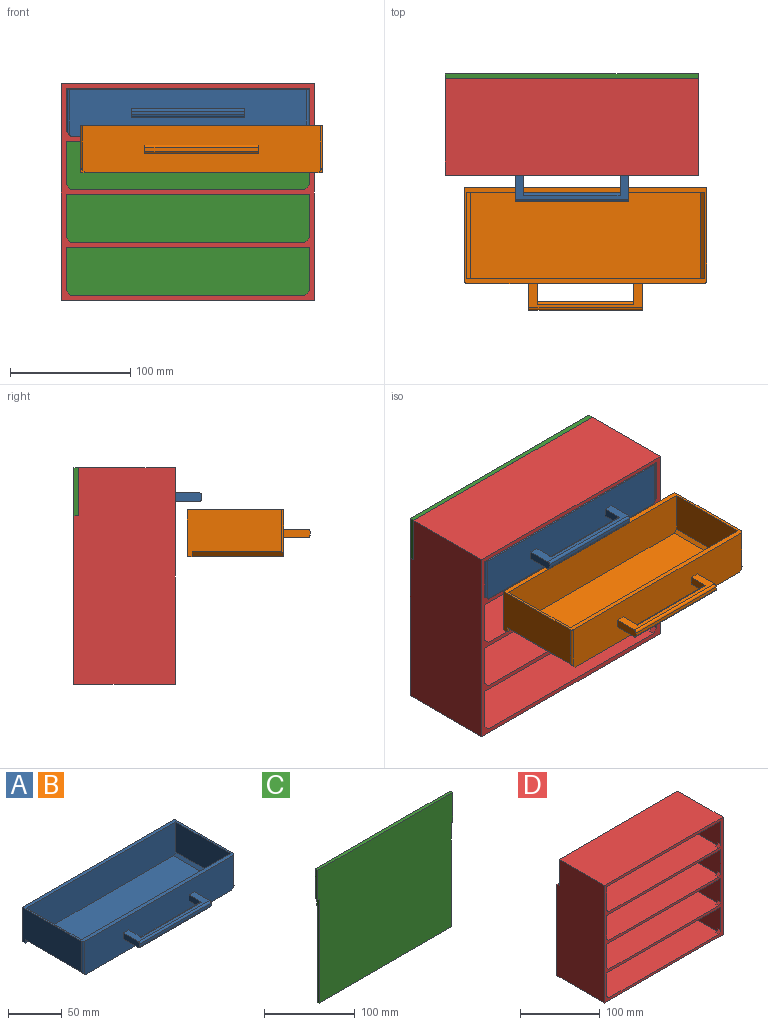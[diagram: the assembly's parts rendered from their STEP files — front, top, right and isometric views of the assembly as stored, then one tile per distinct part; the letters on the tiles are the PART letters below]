
ASSEMBLY  parts=4 mates=2
PART A: 31 faces, bbox 201x102x39 mm
  f0: plane 17x7mm, normal (1,0,0), area 106.7mm2, adj f2,f22,f23,f26,f27,f28
  f1: plane 17x7mm, normal (-1,0,0), area 106.7mm2, adj f2,f22,f23,f26,f27,f28
  f2: plane 197x39mm, normal (0,-1,0), area 7581mm2, adj f0,f1,f8,f10,f11,f12,f19,f20
  f3: plane 72x34.17mm, normal (-1,0,0), area 2460mm2, adj f4,f8,f15,f18
  f4: plane 72x2.83mm, normal (-0.71,0,0.71), area 288.5mm2, adj f3,f5,f15,f18
  f5: plane 191.33x72mm, normal (0,0,1), area 13776mm2, adj f4,f6,f15,f18
  f6: plane 72x2.83mm, normal (0.71,0,0.71), area 288.5mm2, adj f5,f7,f15,f18
  f7: plane 72x34.17mm, normal (1,0,0), area 2460mm2, adj f6,f8,f15,f18
  f8: plane 201x80mm, normal (0,0,1), area 1894.3mm2, adj f2,f3,f7,f9,f13,f15,f16,f18
  f9: plane 78x39mm, normal (-1,0,0), area 2745.6mm2, adj f8,f10,f11,f16,f17,f19
  f10: plane 76x4.01mm, normal (-0.71,0,-0.71), area 429.2mm2, adj f2,f9,f11,f17,f19
  f11: plane 201x80mm, normal (0,0,-1), area 15471.2mm2, adj f2,f9,f10,f12,f13,f14,f16,f17
  f12: plane 76x4.01mm, normal (0.71,0,-0.71), area 429.2mm2, adj f2,f11,f13,f14,f20
  f13: plane 78x39mm, normal (1,0,0), area 2745.6mm2, adj f8,f11,f12,f14,f16,f20
  f14: plane 4.01x4.01mm, normal (0,-1,0), area 8mm2, adj f11,f12,f13
  f15: plane 197x37mm, normal (0,-1,0), area 7281mm2, adj f3,f4,f5,f6,f7,f8
  f16: plane 201x39mm, normal (0,1,0), area 7839mm2, adj f8,f9,f11,f13
  f17: plane 4.01x4.01mm, normal (0,-1,0), area 8mm2, adj f9,f10,f11
  f18: plane 197x37mm, normal (0,1,0), area 7281mm2, adj f3,f4,f5,f6,f7,f8
  f19: cylinder r=2mm len=37mm, axis (0,0,1), area 112.2mm2, adj f2,f8,f9,f10
  f20: cylinder r=2mm len=37mm, axis (0,0,-1), area 112.2mm2, adj f2,f8,f12,f13
  f21: plane 22x7mm, normal (-1,0,0), area 152.3mm2, adj f2,f22,f23,f24,f29,f30
  f22: plane 94x20mm, normal (0,0,-1), area 520mm2, adj f0,f1,f2,f21,f25,f28,f29
  f23: plane 94x20mm, normal (0,0,1), area 520mm2, adj f0,f1,f2,f21,f25,f27,f30
  f24: plane 94x3mm, normal (0,-1,0), area 282mm2, adj f21,f25,f29,f30
  f25: plane 22x7mm, normal (1,0,0), area 152.3mm2, adj f2,f22,f23,f24,f29,f30
  f26: plane 80x3mm, normal (0,1,0), area 240mm2, adj f0,f1,f27,f28
  f27: cylinder r=2mm len=80mm, axis (-1,0,0), area 251.3mm2, adj f0,f1,f23,f26
  f28: cylinder r=2mm len=80mm, axis (1,0,0), area 251.3mm2, adj f0,f1,f22,f26
  f29: cylinder r=2mm len=94mm, axis (-1,0,0), area 295.3mm2, adj f21,f22,f24,f25
  f30: cylinder r=2mm len=94mm, axis (1,0,0), area 295.3mm2, adj f21,f23,f24,f25
PART B: same geometry as A
PART C: 16 faces, bbox 210x4x180 mm
  f0: plane 4x2.01mm, normal (0,0,-1), area 8mm2, adj f3,f5,f6,f11
  f1: plane 40x4mm, normal (-1,0,0), area 160mm2, adj f2,f4,f5,f6
  f2: plane 4x2.01mm, normal (0,0,-1), area 8mm2, adj f1,f5,f6,f12
  f3: plane 40x4mm, normal (1,0,0), area 160mm2, adj f0,f4,f5,f6
  f4: plane 210x4mm, normal (0,0,1), area 840mm2, adj f1,f3,f5,f6
  f5: plane 210x180mm, normal (0,-1,0), area 37238.6mm2, adj f0,f1,f2,f3,f4,f11,f12,f13
  f6: plane 210x180mm, normal (0,1,0), area 36718.6mm2, adj f0,f1,f2,f3,f4,f8,f9,f11
  f7: plane 130x2mm, normal (0,1,0), area 260mm2, adj f8,f12,f13,f15
  f8: plane 130x2mm, normal (-1,0,0), area 259.3mm2, adj f6,f7,f13,f15
  f9: plane 130x2mm, normal (1,0,0), area 259.3mm2, adj f6,f10,f13,f14
  f10: plane 130x2mm, normal (0,1,0), area 260mm2, adj f9,f11,f13,f14
  f11: plane 140x4mm, normal (1,0,0), area 300.7mm2, adj f0,f5,f6,f10,f13,f14
  f12: plane 140x4mm, normal (-1,0,0), area 300.7mm2, adj f2,f5,f6,f7,f13,f15
  f13: plane 205.99x4mm, normal (0,0,-1), area 816mm2, adj f5,f6,f7,f8,f9,f10,f11,f12
  f14: plane 2x2mm, normal (0,0,-1), area 4mm2, adj f6,f9,f10,f11
  f15: plane 2x2mm, normal (0,0,-1), area 4mm2, adj f6,f7,f8,f12
PART D: 50 faces, bbox 210x84x180 mm
  f0: plane 80x40mm, normal (-1,0,0), area 3180mm2, adj f7,f8,f13,f21,f48,f49
  f1: plane 80x40mm, normal (-1,0,0), area 3180mm2, adj f2,f8,f15,f21,f46,f47
  f2: plane 202x80mm, normal (0,0,1), area 16120mm2, adj f1,f8,f14,f21,f44,f45,f46,f47
  f3: plane 80x40mm, normal (-1,0,0), area 3180mm2, adj f6,f8,f17,f21,f42,f43
  f4: plane 80x40mm, normal (-1,0,0), area 3180mm2, adj f5,f8,f19,f21,f40,f41
  f5: plane 202x80mm, normal (0,0,1), area 16120mm2, adj f4,f8,f18,f21,f38,f39,f40,f41
  f6: plane 202x80mm, normal (0,0,1), area 16120mm2, adj f3,f8,f16,f21,f36,f37,f42,f43
  f7: plane 202x80mm, normal (0,0,1), area 16120mm2, adj f0,f8,f12,f21,f34,f35,f48,f49
  f8: plane 210x180mm, normal (0,1,0), area 4920mm2, adj f0,f1,f2,f3,f4,f5,f6,f7
  f9: plane 180x84mm, normal (-1,0,0), area 14960mm2, adj f8,f10,f20,f21,f25,f26
  f10: plane 210x84mm, normal (0,0,-1), area 16824mm2, adj f8,f9,f11,f21,f23,f24,f26,f27
  f11: plane 180x84mm, normal (1,0,0), area 14960mm2, adj f8,f10,f20,f21,f22,f23
  f12: plane 80x40mm, normal (1,0,0), area 3180mm2, adj f7,f8,f13,f21,f34,f35
  f13: plane 202x80mm, normal (0,0,-1), area 16160mm2, adj f0,f8,f12,f21
  f14: plane 80x40mm, normal (1,0,0), area 3180mm2, adj f2,f8,f15,f21,f44,f45
  f15: plane 202x80mm, normal (0,0,-1), area 16160mm2, adj f1,f8,f14,f21
  f16: plane 80x40mm, normal (1,0,0), area 3180mm2, adj f6,f8,f17,f21,f36,f37
  f17: plane 202x80mm, normal (0,0,-1), area 16160mm2, adj f3,f8,f16,f21
  f18: plane 80x40mm, normal (1,0,0), area 3180mm2, adj f5,f8,f19,f21,f38,f39
  f19: plane 202x80mm, normal (0,0,-1), area 16160mm2, adj f4,f8,f18,f21
  f20: plane 210x80mm, normal (0,0,1), area 16800mm2, adj f8,f9,f11,f21
  f21: plane 210x180mm, normal (0,-1,0), area 5544mm2, adj f0,f1,f2,f3,f4,f5,f6,f7
  f22: plane 4x2mm, normal (0,0,1), area 8mm2, adj f8,f11,f23,f24
  f23: plane 140x4mm, normal (0,1,0), area 540mm2, adj f10,f11,f22,f24,f32,f33
  f24: plane 140x4mm, normal (-1,0,0), area 300mm2, adj f8,f10,f22,f23,f31,f32
  f25: plane 4x2mm, normal (0,0,1), area 8mm2, adj f8,f9,f26,f27
  f26: plane 140x4mm, normal (0,1,0), area 540mm2, adj f9,f10,f25,f27,f29,f30
  f27: plane 140x4mm, normal (1,0,0), area 300mm2, adj f8,f10,f25,f26,f28,f29
  f28: plane 130x2mm, normal (0,-1,0), area 260mm2, adj f10,f27,f29,f30
  f29: plane 2x2mm, normal (0,0,1), area 4mm2, adj f26,f27,f28,f30
  f30: plane 130x2mm, normal (1,0,0), area 260mm2, adj f10,f26,f28,f29
  f31: plane 130x2mm, normal (0,-1,0), area 260mm2, adj f10,f24,f32,f33
  f32: plane 2x2mm, normal (0,0,1), area 4mm2, adj f23,f24,f31,f33
  f33: plane 130x2mm, normal (-1,0,0), area 260mm2, adj f10,f23,f31,f32
  f34: plane 5x4mm, normal (0.71,0,0.71), area 28.3mm2, adj f7,f12,f21,f35
  f35: plane 4x4mm, normal (0,1,0), area 8mm2, adj f7,f12,f34
  f36: plane 5x4mm, normal (0.71,0,0.71), area 28.3mm2, adj f6,f16,f21,f37
  f37: plane 4x4mm, normal (0,1,0), area 8mm2, adj f6,f16,f36
  f38: plane 5x4mm, normal (0.71,0,0.71), area 28.3mm2, adj f5,f18,f21,f39
  f39: plane 4x4mm, normal (0,1,0), area 8mm2, adj f5,f18,f38
  f40: plane 5x4mm, normal (-0.71,0,0.71), area 28.3mm2, adj f4,f5,f21,f41
  f41: plane 4x4mm, normal (0,1,0), area 8mm2, adj f4,f5,f40
  f42: plane 5x4mm, normal (-0.71,0,0.71), area 28.3mm2, adj f3,f6,f21,f43
  f43: plane 4x4mm, normal (0,1,0), area 8mm2, adj f3,f6,f42
  f44: plane 5x4mm, normal (0.71,0,0.71), area 28.3mm2, adj f2,f14,f21,f45
  f45: plane 4x4mm, normal (0,1,0), area 8mm2, adj f2,f14,f44
  f46: plane 5x4mm, normal (-0.71,0,0.71), area 28.3mm2, adj f1,f2,f21,f47
  f47: plane 4x4mm, normal (0,1,0), area 8mm2, adj f1,f2,f46
  f48: plane 5x4mm, normal (-0.71,0,0.71), area 28.3mm2, adj f0,f7,f21,f49
  f49: plane 4x4mm, normal (0,1,0), area 8mm2, adj f0,f7,f48
PLACE A t=(-34.82,98.75,59.58)mm
PLACE B t=(-23.4,8.71,29.54)mm
PLACE C t=(-47.58,106.75,38.3)mm
PLACE D t=(-20.29,102.75,0.57)mm
MATE planar A.f11 <-> D.f7  axis (0,0,-1) through (-29.2,22.75,38.6)mm
MATE planar C.f5 <-> D.f8  axis (0,-1,0) through (73.8,102.75,-97.4)mm
